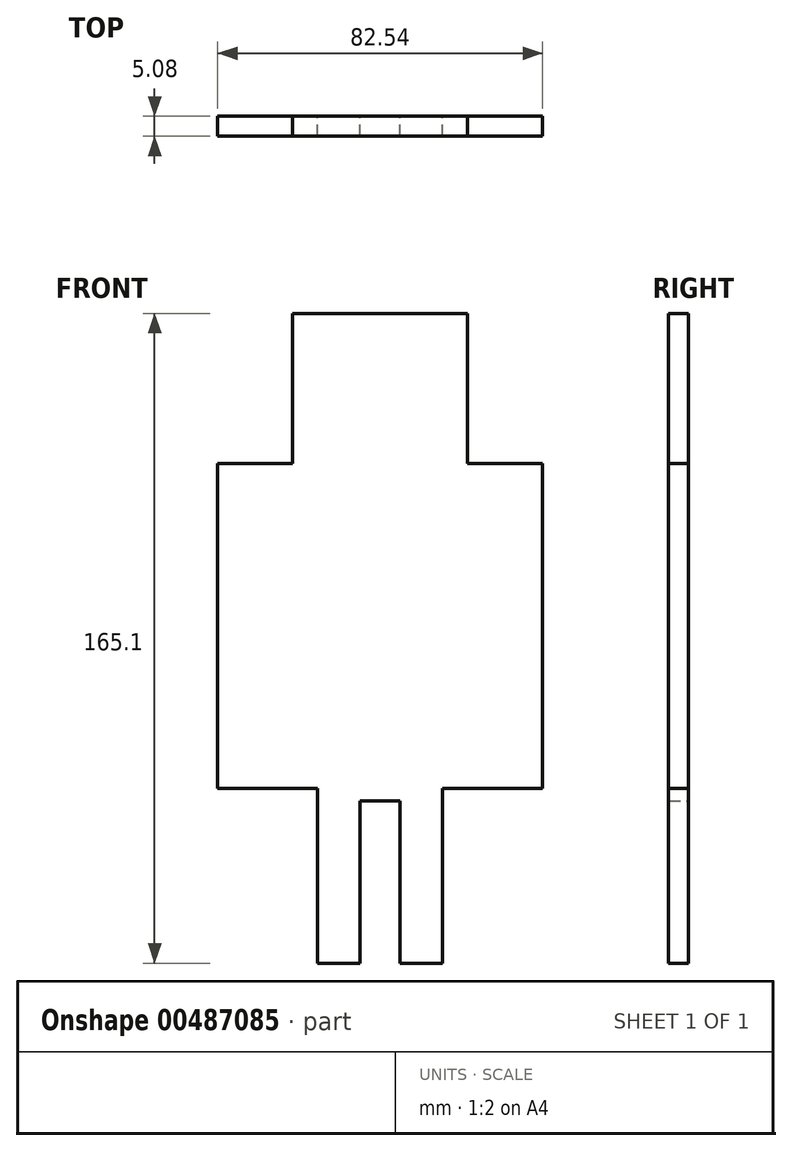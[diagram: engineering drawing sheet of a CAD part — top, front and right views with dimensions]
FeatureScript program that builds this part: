
annotation { "Feature Type Name" : "Feature", "Feature Type Description" : "" }
export const myFeature = defineFeature(function(context is Context, id is Id, definition is map)
    precondition{}
    {
        {
            var Q0;
            Q0=qCreatedBy(makeId("Front.planeOp"),FACE);
            var sketch = newSketch(context, id + "F0", { "sketchPlane" : qUnion([Q0])});
            skLineSegment(sketch, "E0.bottom", {"start": v(-41.28, 0) * mm, "end": v(-22.23, 0) * mm});
            skLineSegment(sketch, "E0.top", {"start": v(-41.28, -82.55) * mm, "end": v(-15.87, -82.55) * mm});
            skLineSegment(sketch, "E0.left", {"start": v(-41.28, 0) * mm, "end": v(-41.27, -82.55) * mm});
            skLineSegment(sketch, "E0.right", {"start": v(41.28, 0) * mm, "end": v(41.28, -82.55) * mm});
            skLineSegment(sketch, "E1.top", {"start": v(-22.23, 38.1) * mm, "end": v(22.22, 38.1) * mm});
            skLineSegment(sketch, "E1.left", {"start": v(-22.23, 0) * mm, "end": v(-22.23, 38.1) * mm});
            skLineSegment(sketch, "E1.right", {"start": v(22.23, 0) * mm, "end": v(22.22, 38.1) * mm});
            skLineSegment(sketch, "E2.trimOffspring", {"start": v(22.23, 0) * mm, "end": v(41.28, 0) * mm});
            skLineSegment(sketch, "E3.top", {"start": v(-15.87, -127) * mm, "end": v(-5.08, -127) * mm});
            skLineSegment(sketch, "E3.left", {"start": v(-15.87, -82.55) * mm, "end": v(-15.87, -127) * mm});
            skLineSegment(sketch, "E3.right", {"start": v(15.88, -82.55) * mm, "end": v(15.88, -127) * mm});
            skLineSegment(sketch, "E4.top", {"start": v(-5.08, -85.72) * mm, "end": v(5.08, -85.72) * mm});
            skLineSegment(sketch, "E4.left", {"start": v(-5.08, -127) * mm, "end": v(-5.08, -85.72) * mm});
            skLineSegment(sketch, "E4.right", {"start": v(5.08, -127) * mm, "end": v(5.08, -85.72) * mm});
            skLineSegment(sketch, "E5.trimOffspring", {"start": v(15.88, -82.55) * mm, "end": v(41.28, -82.55) * mm});
            skLineSegment(sketch, "E6.trimOffspring", {"start": v(5.08, -127) * mm, "end": v(15.88, -127) * mm});
            skSolve(sketch);
        }
        {
            var Q0;
            Q0=makeQuery(id+"F0.imprint","IMPRINT",FACE,{"disambiguationData":[TD([[makeQuery(id+"F0.imprint","IMPRINT",EDGE,{"derivedFrom":sQuery(id+"F0.wireOp",EDGE,"E0.bottom")}),-1.0]])]});
            extrude(context, id + "F1", {"entities" : qUnion([Q0]), "depth" : 5.08 * mm});
        }
    });
